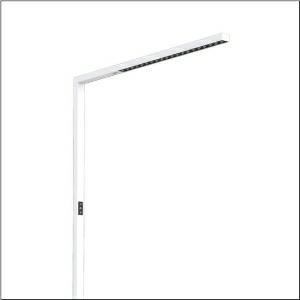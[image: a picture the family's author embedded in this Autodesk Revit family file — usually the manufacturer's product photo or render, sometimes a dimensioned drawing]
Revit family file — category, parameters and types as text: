
# Revit family: silica_31_floor_51my52fa3cw
name_source: partatom
category: Lighting Fixtures
units: mm (PartAtom-declared; Revit-internal decimal feet)

## family parameters
Cut with Voids When Loaded = No
Host = Face
Light Source = No
Part Type = Normal
Room Calculation Point = No
Round Connector Dimension = Use Diameter
Shared = No

## types (1)
- Silica 31 Floor (1 x LED, 10300 lm, 75 W, 3000K)
    Apparent Load = 75 VA
    CIE Flux Codes = 86 100 100 24 100
    Color Rendering = 80
    Color Temperature = 3000K
    Default Elevation = 1800 mm
    Description = Silica® 31 Floor, floorstanding luminaire, secondary optical cover: cover panel, of PMMA, light emission: direct/indirect distribution, primary light characteristic: symmetric, installation type: not mounted, LED, rated luminous flux: 10.300lm, luminous efficacy: 137lm/W, light colour: 830, colour temperature: 3000K, control gear: Touchdim, daylight-dependent control, with cable with plug, mains connection: 230V, AC, 50Hz, connection cable included, cable length: 2,5m, rated input power: 75W, luminaire head, of aluminium, traffic white (RAL 9016), length: 1.203mm, width: 52mm, supporting column, angular, of aluminium, traffic white (RAL 9016), baseplate, of steel, traffic white (RAL 9016), local control - self-sufficient standalone sensors, direct and indirect component separately switchable, protection rating (complete): IP20, insulation class (complete): insulation class I (protective earthing), certification: CE, ENEC, permissible operating ambient temperature: -20..+40°C, standard: EN 50419, packaging unit: 1 piece
    Height = 36 mm
    Lamp = 1 x LED
    Lamp Light Flux = 10300 lm
    Lamp Power = 75 W
    Lamp count = 1
    Length = 1203 mm
    Luminous efficacy = 137 lm/W
    Manufacturer = Siteco
    ModVariant = No
    Model = 51MY52FA3CW
    Mounting Place = Floor
    Mounting Type = Freestanding
    Number of Poles = 1
    OnlyDefault = Yes
    Power Factor = 1
    Product Name = Silica 31 Floor
    Product group = floorstanding luminaire
    ProductGroupID = 1302
    Protection Class = Protection class I
    Protection Degree = IP 20
    RLX_Detail_Level = 1
    RLX_Emergency_Light_Flux = 0 lm
    RLX_Emergency_Type = 0
    RLX_Emergency_Type_DB = No
    RlxData = <blob elided: 17293 chars, md5=05c286f8>
    Socket = socket
    Standby Power = 0 W
    System Light Flux = 10300 lm
    System Power = 75 W
    Type Comments = Product without accessories
    Type Image = l_1275309.jpg
    URL = http://relux.com
    VarID = ---
    Voltage = 0 V
    Weight = 0.00 kg
    Width = 52 mm  [stored 0.170604 ft]

note: [stored X ft] marks values corroborated as IEEE doubles in the binary element streams (Revit-internal decimal feet)

## geometry (parser evidence)
native form markers: Blend x4, Sweep x15
no freeform markers — native parametric forms only
